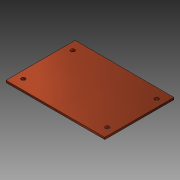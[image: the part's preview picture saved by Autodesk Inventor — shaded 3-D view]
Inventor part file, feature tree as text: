
AUTODESK INVENTOR PART (.ipt)
format: ipt  version: 2018 (Build 220112000, 112)  size: 89,088 bytes
history: native  units: mm
features: other x3, reference x2, extrude x1, sketch x1
ambient origin geometry x8: Origin, YZ Plane, XZ Plane, XY Plane, X Axis, Y Axis, Z Axis, Center Point
bodies: Solid1 (feature_tree)
feature tree (7):
  extrude  "Extrusion1"  Depth=70.0mm
  sketch  "Sketch1"  dims[d0=100.0mm d1=70.0mm d2=2.0mm d3=0.0mm]
  reference  "Reference1"
  reference  "Reference2"
  other  "Assembly1"
  other  "Dock_Pedal:4"
  other  "Dock_Pedal:5"
